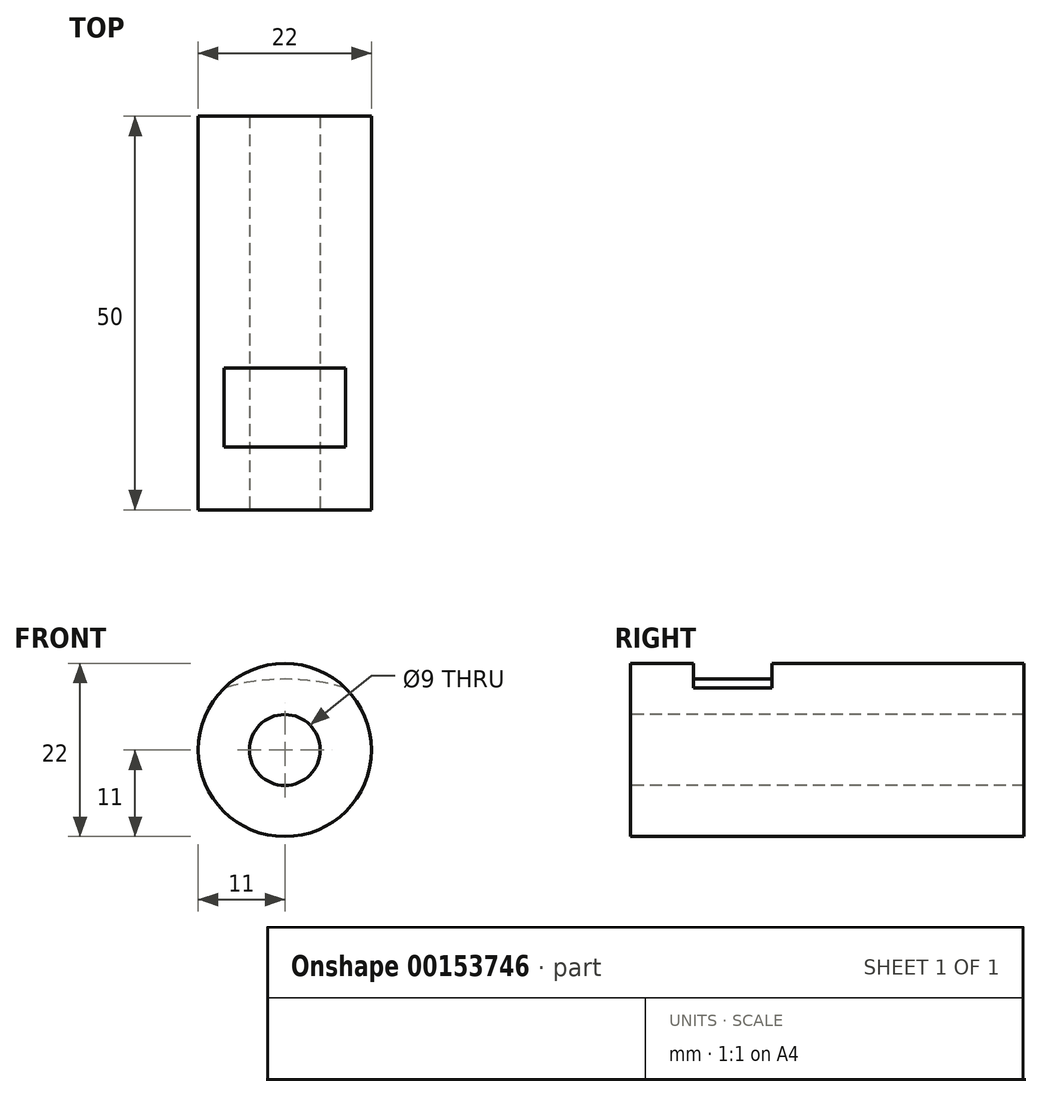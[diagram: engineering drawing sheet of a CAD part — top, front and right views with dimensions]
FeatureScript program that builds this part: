
annotation { "Feature Type Name" : "Feature", "Feature Type Description" : "" }
export const myFeature = defineFeature(function(context is Context, id is Id, definition is map)
    precondition{}
    {
        {
            var Q0;
            Q0=qCreatedBy(makeId("Front.planeOp"),FACE);
            var sketch = newSketch(context, id + "F0", { "sketchPlane" : qUnion([Q0])});
            skCircle(sketch, "E0", {"center": v(0, 0) * mm, "radius": 11 * mm});
            skCircle(sketch, "E1", {"center": v(0, 0) * mm, "radius": 4.5 * mm});
            skLineSegment(sketch, "E2", {"start": v(0, 0) * mm, "end": v(0, -17.5) * mm});
            skArc(sketch, "E3", {"start": v(7.7, 7.86) * mm, "mid": v(0, 9) * mm, "end": v(-7.7, 7.86) * mm});
            skSolve(sketch);
        }
        {
            var Q0;
            Q0=qSketchRegion(id+"F0",true);
            extrude(context, id + "F1", {"entities" : qUnion([Q0]), "oppositeDirection" : true, "depth" : 8 * mm});
        }
        {
            var Q0;
            Q0=makeQuery(id+"F0.imprint","IMPRINT",FACE,{"disambiguationData":[TD([[makeQuery(id+"F0.imprint","IMPRINT",EDGE,{"derivedFrom":sQuery(id+"F0.wireOp",EDGE,"E1")}),-1.0]])]});
            extrude(context, id + "F2", {"entities" : qUnion([Q0]), "operationType" : NewBodyOperationType.ADD, "oppositeDirection" : true, "depth" : 18 * mm});
        }
        {
            var Q0;
            Q0=makeQuery(id+"F0.imprint","IMPRINT",FACE,{"disambiguationData":[TD([[makeQuery(id+"F0.imprint","IMPRINT",EDGE,{"derivedFrom":sQuery(id+"F0.wireOp",EDGE,"E1")}),-1.0]])]});
            var Q1;
            {var subQ0=sQuery(id+"F0.wireOp",EDGE,"E3");Q1=makeQuery(id+"F0.imprint","IMPRINT",FACE,{"disambiguationData":[TD([[makeQuery(id+"F0.imprint","IMPRINT",EDGE,{"derivedFrom":subQ0}),-1.0]])]});}
            var Q2;
            Q2=sQuery(id+"F0.wireOp",EDGE,"E0");
            var Q3;
            Q3=sQuery(id+"F0.wireOp",EDGE,"E1");
            extrude(context, id + "F3", {"entities" : qUnion([Q0, Q1]), "operationType" : NewBodyOperationType.ADD, "surfaceEntities" : qUnion([Q2, Q3]), "oppositeDirection" : true, "depth" : 50 * mm, "hasSecondDirection" : true, "secondDirectionOppositeDirection" : true, "secondDirectionDepth" : 18 * mm});
        }
    });
